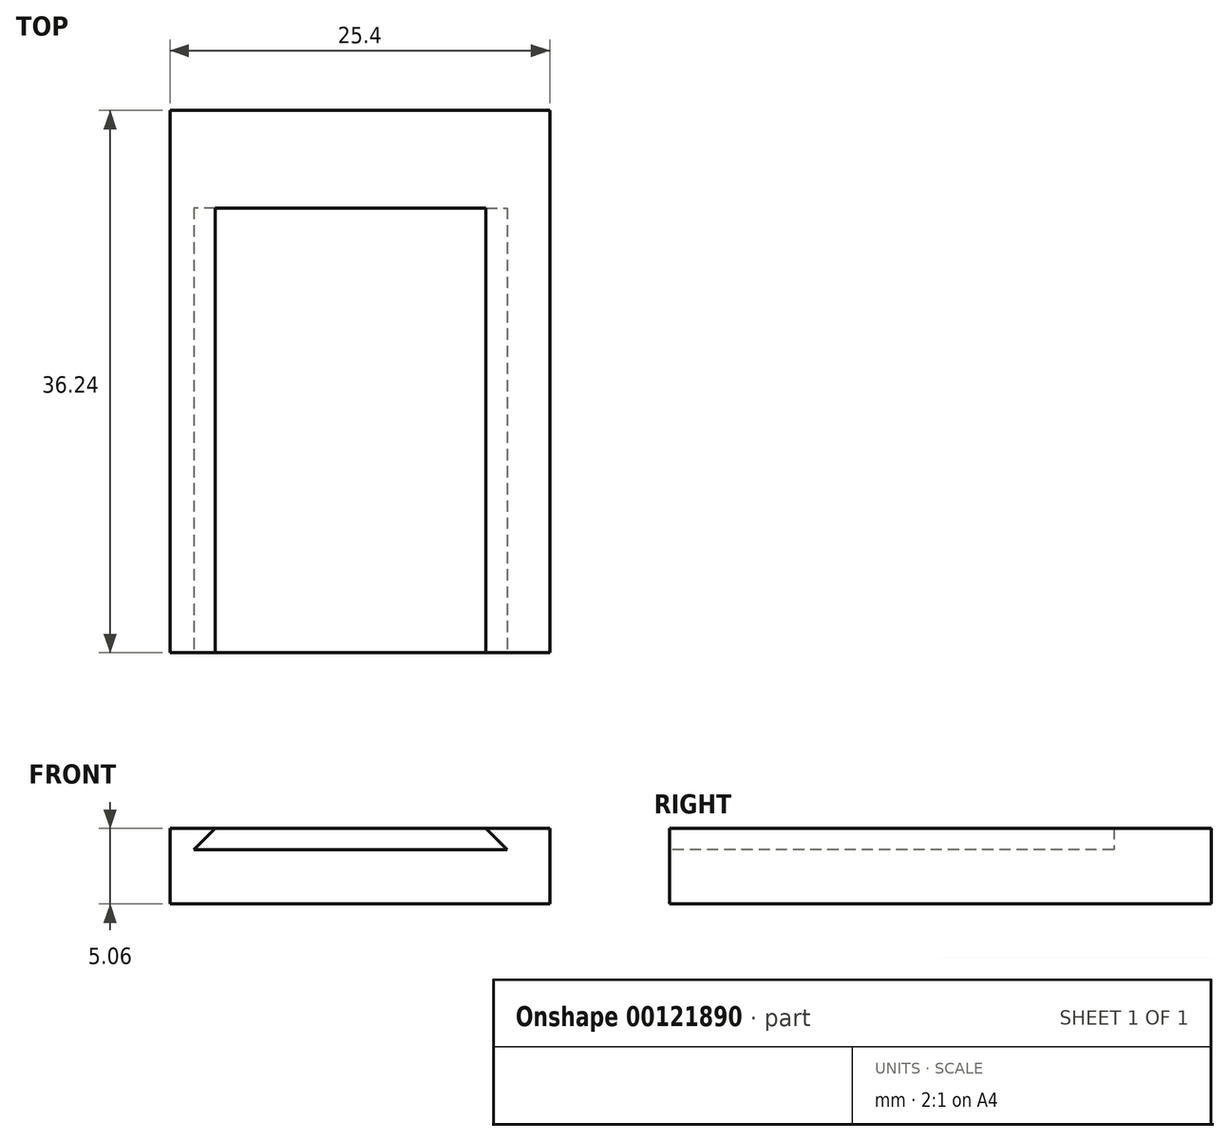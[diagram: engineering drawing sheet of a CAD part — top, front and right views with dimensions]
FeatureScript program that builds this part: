
annotation { "Feature Type Name" : "Feature", "Feature Type Description" : "" }
export const myFeature = defineFeature(function(context is Context, id is Id, definition is map)
    precondition{}
    {
        {
            var Q0;
            Q0=qCreatedBy(makeId("Front.planeOp"),FACE);
            var sketch = newSketch(context, id + "F0", { "sketchPlane" : qUnion([Q0])});
            skLineSegment(sketch, "E0.bottom", {"start": v(-12.7, 2.53) * mm, "end": v(12.7, 2.53) * mm});
            skLineSegment(sketch, "E0.top", {"start": v(-12.7, -2.53) * mm, "end": v(12.7, -2.53) * mm});
            skLineSegment(sketch, "E0.left", {"start": v(-12.7, 2.53) * mm, "end": v(-12.7, -2.53) * mm});
            skLineSegment(sketch, "E0.right", {"start": v(12.7, 2.53) * mm, "end": v(12.7, -2.53) * mm});
            skPoint(sketch, "E0.middle", {"position": v(0, 0) * mm});
            skSolve(sketch);
        }
        {
            var Q0;
            Q0=makeQuery(id+"F0.imprint","IMPRINT",FACE,{"disambiguationData":[TD([[makeQuery(id+"F0.imprint","IMPRINT",EDGE,{"derivedFrom":sQuery(id+"F0.wireOp",EDGE,"E0.bottom")}),-1.0]])]});
            var sketch = newSketch(context, id + "F1", { "sketchPlane" : qUnion([Q0])});
            skLineSegment(sketch, "E1", {"start": v(-9.1, 3.1) * mm, "end": v(-11.1, 1.1) * mm});
            skLineSegment(sketch, "E2", {"start": v(-11.1, 1.1) * mm, "end": v(9.87, 1.1) * mm});
            skLineSegment(sketch, "E3", {"start": v(9.87, 1.1) * mm, "end": v(7.87, 3.1) * mm});
            skLineSegment(sketch, "E4", {"start": v(7.87, 3.1) * mm, "end": v(-9.1, 3.1) * mm});
            skSolve(sketch);
        }
        {
            var Q0;
            Q0=makeQuery(id+"F0.imprint","IMPRINT",FACE,{"disambiguationData":[TD([[makeQuery(id+"F0.imprint","IMPRINT",EDGE,{"derivedFrom":sQuery(id+"F0.wireOp",EDGE,"E0.bottom")}),-1.0]])]});
            extrude(context, id + "F2", {"entities" : qUnion([Q0]), "oppositeDirection" : true, "depth" : 36.24 * mm});
        }
        {
            var Q0;
            {var subQ0=sQuery(id+"F1.wireOp",EDGE,"E2");Q0=makeQuery(id+"F1.imprint","IMPRINT",FACE,{"disambiguationData":[TD([[makeQuery(id+"F1.imprint","IMPRINT",EDGE,{"derivedFrom":subQ0}),1.0]])]});}
            extrude(context, id + "F3", {"entities" : qUnion([Q0]), "operationType" : NewBodyOperationType.REMOVE, "oppositeDirection" : true, "depth" : 29.72 * mm});
        }
    });
